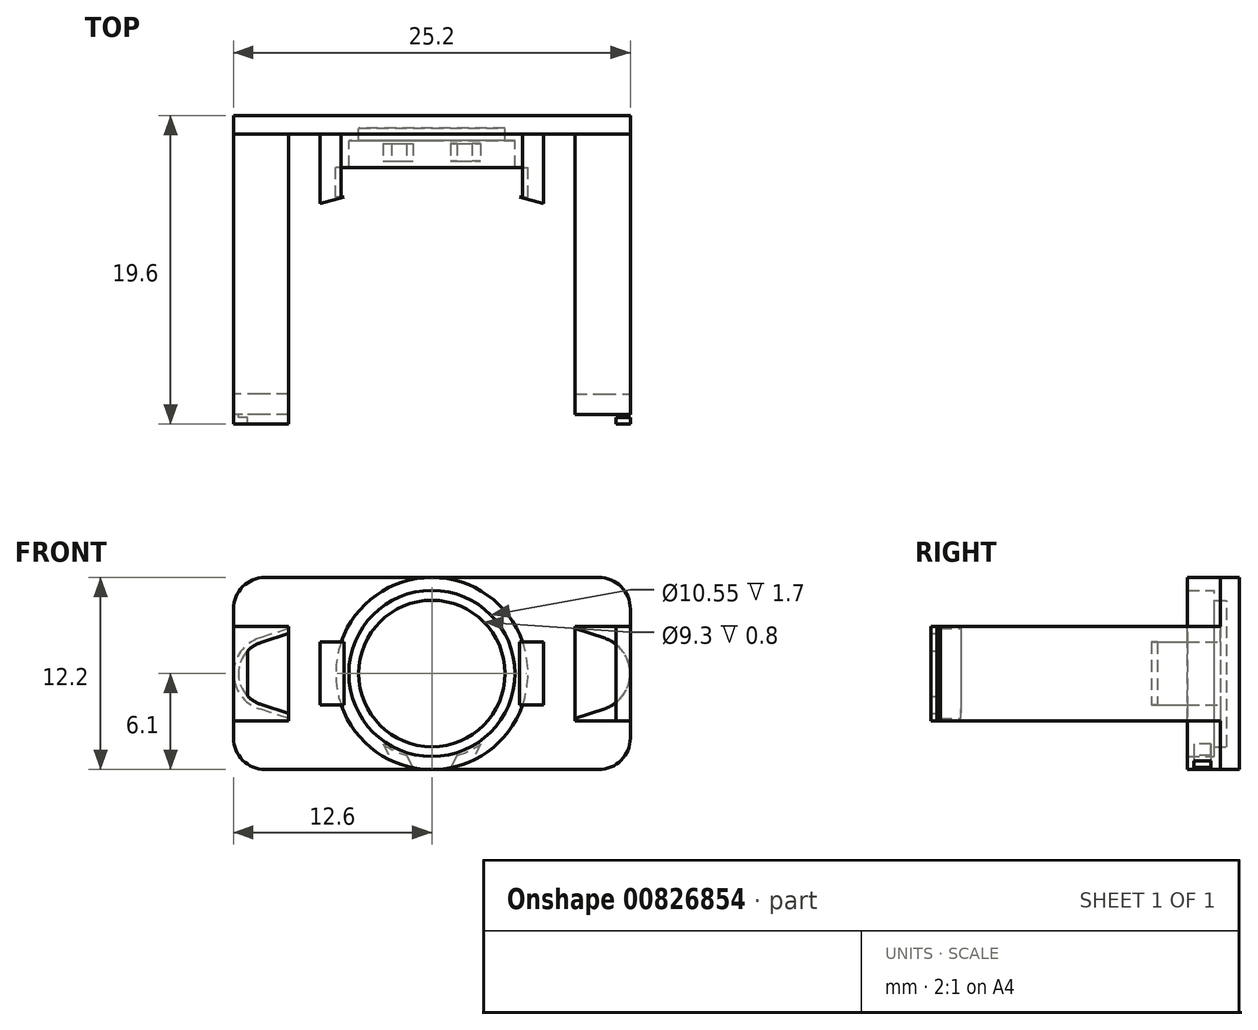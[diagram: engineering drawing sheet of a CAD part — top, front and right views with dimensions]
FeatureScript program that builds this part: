
annotation { "Feature Type Name" : "Feature", "Feature Type Description" : "" }
export const myFeature = defineFeature(function(context is Context, id is Id, definition is map)
    precondition{}
    {
        {
            var Q0;
            Q0=qCreatedBy(makeId("Front.planeOp"),FACE);
            var sketch = newSketch(context, id + "F0", { "sketchPlane" : qUnion([Q0])});
            skCircle(sketch, "E0", {"center": v(0, 0) * mm, "radius": 5 * mm});
            skCircle(sketch, "E1", {"center": v(0, 0) * mm, "radius": 6.1 * mm});
            skSolve(sketch);
        }
        {
            var Q0;
            Q0=makeQuery(id+"F0.imprint","IMPRINT",FACE,{"disambiguationData":[TD([[makeQuery(id+"F0.imprint","IMPRINT",EDGE,{"derivedFrom":sQuery(id+"F0.wireOp",EDGE,"E0")}),-1.0]])]});
            var Q1;
            Q1=makeQuery(id+"F0.imprint","IMPRINT",FACE,{"disambiguationData":[TD([[makeQuery(id+"F0.imprint","IMPRINT",EDGE,{"derivedFrom":sQuery(id+"F0.wireOp",EDGE,"E0")}),1.0]])]});
            extrude(context, id + "F1", {"entities" : qUnion([Q0, Q1]), "depth" : 0.8 * mm, "offsetDistance" : 25 * mm});
        }
        {
            var Q0;
            Q0=makeQuery(id+"F1.opExtrude","CAP_FACE",FACE,{"disambiguationData":[OSD([sQuery(id+"F0.wireOp",EDGE,"E1")])],"isStart":false});
            var sketch = newSketch(context, id + "F2", { "sketchPlane" : qUnion([Q0])});
            skCircle(sketch, "E2", {"center": v(0, 0) * mm, "radius": 5.45 * mm});
            skCircle(sketch, "E3", {"center": v(0, 0) * mm, "radius": 6.1 * mm});
            skSolve(sketch);
        }
        {
            var Q0;
            Q0=makeQuery(id+"F2.imprint","IMPRINT",FACE,{"disambiguationData":[TD([[makeQuery(id+"F2.imprint","IMPRINT",EDGE,{"derivedFrom":sQuery(id+"F2.wireOp",EDGE,"E2")}),-1.0]])]});
            extrude(context, id + "F3", {"entities" : qUnion([Q0]), "operationType" : NewBodyOperationType.ADD, "depth" : 2.5 * mm, "offsetDistance" : 25 * mm});
        }
        {
            var Q0;
            Q0=makeQuery(id+"F1.opExtrude","CAP_FACE",FACE,{"disambiguationData":[OSD([sQuery(id+"F0.wireOp",EDGE,"E1")])],"isStart":false});
            var sketch = newSketch(context, id + "F4", { "sketchPlane" : qUnion([Q0])});
            skCircle(sketch, "E4", {"center": v(0, 0) * mm, "radius": 4.65 * mm});
            skSolve(sketch);
        }
        {
            var Q0;
            Q0=makeQuery(id+"F4.imprint","IMPRINT",FACE,{"disambiguationData":[TD([[makeQuery(id+"F4.imprint","IMPRINT",EDGE,{"derivedFrom":sQuery(id+"F4.wireOp",EDGE,"E4")}),-1.0]])]});
            extrude(context, id + "F5", {"entities" : qUnion([Q0]), "operationType" : NewBodyOperationType.ADD, "depth" : 0.8 * mm, "offsetDistance" : 25 * mm});
        }
        {
            var Q0;
            Q0=makeQuery(id+"F3.opExtrude","CAP_FACE",FACE,{"disambiguationData":[OSD([sQuery(id+"F2.wireOp",EDGE,"E2"),sQuery(id+"F2.wireOp",EDGE,"E3")])],"isStart":false});
            var sketch = newSketch(context, id + "F6", { "sketchPlane" : qUnion([Q0])});
            skLineSegment(sketch, "E5", {"start": v(-1.6, -5.2) * mm, "end": v(-1.2, -5.98) * mm});
            skLineSegment(sketch, "E6", {"start": v(-3.1, -4.48) * mm, "end": v(-2.56, -5.54) * mm});
            skLineSegment(sketch, "E7.MirrorCS", {"start": v(1.6, -5.2) * mm, "end": v(1.2, -5.98) * mm});
            skLineSegment(sketch, "E8.MirrorCS", {"start": v(3.1, -4.48) * mm, "end": v(2.56, -5.54) * mm});
            skCircle(sketch, "E9.0", {"center": v(0, 0) * mm, "radius": 5.45 * mm});
            skSolve(sketch);
        }
        {
            var Q0;
            {var subQ0=sQuery(id+"F6.wireOp",EDGE,"E5");Q0=makeQuery(id+"F6.imprint","IMPRINT",FACE,{"disambiguationData":[TD([[makeQuery(id+"F6.imprint","IMPRINT",EDGE,{"derivedFrom":subQ0}),-1.0]])]});}
            var Q1;
            {var subQ0=sQuery(id+"F6.wireOp",EDGE,"E7.MirrorCS");Q1=makeQuery(id+"F6.imprint","IMPRINT",FACE,{"disambiguationData":[TD([[makeQuery(id+"F6.imprint","IMPRINT",EDGE,{"derivedFrom":subQ0}),1.0]])]});}
            extrude(context, id + "F7", {"entities" : qUnion([Q0, Q1]), "operationType" : NewBodyOperationType.REMOVE, "oppositeDirection" : true, "depth" : 1.5 * mm, "offsetDistance" : 25 * mm});
        }
        {
            var Q0;
            {var subQ0=sQuery(id+"F2.wireOp",EDGE,"E3");var subQ1=sQuery(id+"F2.wireOp",EDGE,"E2");Q0=makeQuery(id+"F7.boolean.opBoolean","SPLIT",FACE,{"disambiguationData":[TD([makeQuery(id+"F7.opExtrude","SWEPT_FACE",FACE,{"disambiguationData":[OSD([sQuery(id+"F6.wireOp",EDGE,"E6")])]})])],"derivedFrom":makeQuery(id+"F3.opExtrude","CAP_FACE",FACE,{"disambiguationData":[OSD([subQ1,subQ0])],"isStart":false})});}
            var sketch = newSketch(context, id + "F8", { "sketchPlane" : qUnion([Q0])});
            skArc(sketch, "E10", {"start": v(-2.56, -5.54) * mm, "mid": v(-1.9, -5.8) * mm, "end": v(-1.2, -5.98) * mm});
            skLineSegment(sketch, "E11", {"start": v(-3.1, -4.48) * mm, "end": v(-2.56, -5.54) * mm});
            skLineSegment(sketch, "E12", {"start": v(-1.6, -5.2) * mm, "end": v(-1.2, -5.98) * mm});
            skLineSegment(sketch, "E13.MirrorCS", {"start": v(3.1, -4.48) * mm, "end": v(2.56, -5.54) * mm});
            skArc(sketch, "E14.MirrorCS", {"start": v(2.56, -5.54) * mm, "mid": v(1.9, -5.8) * mm, "end": v(1.2, -5.98) * mm});
            skLineSegment(sketch, "E15.MirrorCS", {"start": v(1.6, -5.2) * mm, "end": v(1.2, -5.98) * mm});
            skPoint(sketch, "E16.MirrorCS.end.orphan", {"position": v(1.6, -5.2) * mm});
            skPoint(sketch, "E16.MirrorCS.start.orphan", {"position": v(3.1, -4.48) * mm});
            skPoint(sketch, "E17.MirrorCS.end.orphan", {"position": v(-3.1, -4.48) * mm});
            skPoint(sketch, "E17.MirrorCS.start.orphan", {"position": v(-1.6, -5.2) * mm});
            skSolve(sketch);
        }
        {
            var Q0;
            {var subQ0=sQuery(id+"F6.wireOp",EDGE,"E5");Q0=makeQuery(id+"F6.imprint","IMPRINT",FACE,{"disambiguationData":[TD([[makeQuery(id+"F6.imprint","IMPRINT",EDGE,{"derivedFrom":subQ0}),-1.0]])]});}
            var Q1;
            {var subQ0=sQuery(id+"F6.wireOp",EDGE,"E7.MirrorCS");Q1=makeQuery(id+"F6.imprint","IMPRINT",FACE,{"disambiguationData":[TD([[makeQuery(id+"F6.imprint","IMPRINT",EDGE,{"derivedFrom":subQ0}),1.0]])]});}
            extrude(context, id + "F9", {"entities" : qUnion([Q0, Q1]), "operationType" : NewBodyOperationType.ADD, "oppositeDirection" : true, "depth" : 0.4 * mm, "offsetDistance" : 25 * mm});
        }
        {
            var Q0;
            Q0=makeQuery(id+"F1.opExtrude","CAP_FACE",FACE,{"disambiguationData":[OSD([sQuery(id+"F0.wireOp",EDGE,"E1")])],"isStart":true});
            var sketch = newSketch(context, id + "F10", { "sketchPlane" : qUnion([Q0])});
            skLineSegment(sketch, "E18.bottom", {"start": v(-12.6, -6.1) * mm, "end": v(12.6, -6.1) * mm});
            skLineSegment(sketch, "E18.top", {"start": v(-12.6, 6.1) * mm, "end": v(12.6, 6.1) * mm});
            skLineSegment(sketch, "E18.left", {"start": v(-12.6, -6.1) * mm, "end": v(-12.6, 6.1) * mm});
            skLineSegment(sketch, "E18.right", {"start": v(12.6, -6.1) * mm, "end": v(12.6, 6.1) * mm});
            skPoint(sketch, "E18.middle", {"position": v(0, 0) * mm});
            skSolve(sketch);
        }
        {
            var Q0;
            {var subQ0=sQuery(id+"F10.wireOp",EDGE,"E18.right");Q0=makeQuery(id+"F10.imprint","IMPRINT",FACE,{"disambiguationData":[TD([[makeQuery(id+"F10.imprint","IMPRINT",EDGE,{"derivedFrom":subQ0}),1.0]])]});}
            var Q1;
            {var subQ0=sQuery(id+"F10.wireOp",EDGE,"E18.left");Q1=makeQuery(id+"F10.imprint","IMPRINT",FACE,{"disambiguationData":[TD([[makeQuery(id+"F10.imprint","IMPRINT",EDGE,{"derivedFrom":subQ0}),-1.0]])]});}
            extrude(context, id + "F11", {"entities" : qUnion([Q0, Q1]), "operationType" : NewBodyOperationType.ADD, "oppositeDirection" : true, "depth" : 1.2 * mm, "offsetDistance" : 25 * mm});
        }
        {
            var Q0;
            Q0=makeQuery(id+"F11.opExtrude","SWEPT_EDGE",EDGE,{"disambiguationData":[OSD([sQuery(id+"F10.wireOp",EDGE,"E18.bottom"),sQuery(id+"F10.wireOp",EDGE,"E18.right")])]});
            var Q1;
            Q1=makeQuery(id+"F11.opExtrude","SWEPT_EDGE",EDGE,{"disambiguationData":[OSD([sQuery(id+"F10.wireOp",EDGE,"E18.bottom"),sQuery(id+"F10.wireOp",EDGE,"E18.left")])]});
            var Q2;
            Q2=makeQuery(id+"F11.opExtrude","SWEPT_EDGE",EDGE,{"disambiguationData":[OSD([sQuery(id+"F10.wireOp",EDGE,"E18.top"),sQuery(id+"F10.wireOp",EDGE,"E18.left")])]});
            var Q3;
            Q3=makeQuery(id+"F11.opExtrude","SWEPT_EDGE",EDGE,{"disambiguationData":[OSD([sQuery(id+"F10.wireOp",EDGE,"E18.top"),sQuery(id+"F10.wireOp",EDGE,"E18.right")])]});
            fillet(context, id + "F12", {"entities" : qUnion([Q0, Q1, Q2, Q3]), "radius" : 2 * mm, "tangentPropagation" : true, "allowEdgeOverflow" : false});
        }
        {
            var Q0;
            Q0=makeQuery(id+"F11.opExtrude","CAP_FACE",FACE,{"disambiguationData":[OSD([sQuery(id+"F0.wireOp",EDGE,"E1"),sQuery(id+"F10.wireOp",EDGE,"E18.bottom"),sQuery(id+"F10.wireOp",EDGE,"E18.top"),sQuery(id+"F10.wireOp",EDGE,"E18.right")])],"isStart":false});
            var sketch = newSketch(context, id + "F13", { "sketchPlane" : qUnion([Q0])});
            skLineSegment(sketch, "E19", {"start": v(-12.6, 3) * mm, "end": v(-9.1, 3) * mm});
            skLineSegment(sketch, "E20", {"start": v(-9.1, 3) * mm, "end": v(-9.1, -3) * mm});
            skLineSegment(sketch, "E21", {"start": v(-9.1, -3) * mm, "end": v(-12.6, -3) * mm});
            skLineSegment(sketch, "E22", {"start": v(-7.1, 2) * mm, "end": v(-7.1, -2) * mm});
            skLineSegment(sketch, "E23", {"start": v(-7.1, -2) * mm, "end": v(-5.76, -2) * mm});
            skLineSegment(sketch, "E24", {"start": v(-7.1, 2) * mm, "end": v(-5.76, 2) * mm});
            skSolve(sketch);
        }
        {
            var Q0;
            {var subQ0=sQuery(id+"F13.wireOp",EDGE,"E19");Q0=makeQuery(id+"F13.imprint","IMPRINT",FACE,{"disambiguationData":[TD([[makeQuery(id+"F13.imprint","IMPRINT",EDGE,{"derivedFrom":subQ0}),-1.0]])]});}
            extrude(context, id + "F14", {"entities" : qUnion([Q0]), "operationType" : NewBodyOperationType.ADD, "depth" : 16.5 * mm, "offsetDistance" : 25 * mm});
        }
        {
            var Q0;
            Q0=makeQuery(id+"F11.opExtrude","CAP_FACE",FACE,{"disambiguationData":[OSD([sQuery(id+"F0.wireOp",EDGE,"E1"),sQuery(id+"F10.wireOp",EDGE,"E18.bottom"),sQuery(id+"F10.wireOp",EDGE,"E18.top"),sQuery(id+"F10.wireOp",EDGE,"E18.left")])],"isStart":false});
            var sketch = newSketch(context, id + "F15", { "sketchPlane" : qUnion([Q0])});
            skLineSegment(sketch, "E25", {"start": v(12.6, 3) * mm, "end": v(9.1, 3) * mm});
            skLineSegment(sketch, "E26", {"start": v(9.1, 3) * mm, "end": v(9.1, -3) * mm});
            skLineSegment(sketch, "E27", {"start": v(9.1, -3) * mm, "end": v(12.6, -3) * mm});
            skLineSegment(sketch, "E28", {"start": v(7.1, 2) * mm, "end": v(7.1, -2) * mm});
            skLineSegment(sketch, "E29", {"start": v(7.1, -2) * mm, "end": v(5.76, -2) * mm});
            skLineSegment(sketch, "E30", {"start": v(7.1, 2) * mm, "end": v(5.76, 2) * mm});
            skSolve(sketch);
        }
        {
            var Q0;
            {var subQ0=sQuery(id+"F15.wireOp",EDGE,"E25");Q0=makeQuery(id+"F15.imprint","IMPRINT",FACE,{"disambiguationData":[TD([[makeQuery(id+"F15.imprint","IMPRINT",EDGE,{"derivedFrom":subQ0}),1.0]])]});}
            extrude(context, id + "F16", {"entities" : qUnion([Q0]), "operationType" : NewBodyOperationType.ADD, "depth" : 16.5 * mm, "offsetDistance" : 25 * mm});
        }
        {
            var Q0;
            Q0=makeQuery(id+"F15.imprint","IMPRINT",FACE,{"disambiguationData":[TD([[makeQuery(id+"F15.imprint","IMPRINT",EDGE,{"derivedFrom":sQuery(id+"F15.wireOp",EDGE,"E28")}),-1.0]])]});
            var Q1;
            Q1=makeQuery(id+"F13.imprint","IMPRINT",FACE,{"disambiguationData":[TD([[makeQuery(id+"F13.imprint","IMPRINT",EDGE,{"derivedFrom":sQuery(id+"F13.wireOp",EDGE,"E22")}),1.0]])]});
            extrude(context, id + "F17", {"entities" : qUnion([Q0, Q1]), "operationType" : NewBodyOperationType.ADD, "depth" : 4 * mm, "offsetDistance" : 25 * mm});
        }
        {
            var Q0;
            Q0=makeQuery(id+"F17.opExtrude","SWEPT_FACE",FACE,{"disambiguationData":[OSD([sQuery(id+"F13.wireOp",EDGE,"E23")])]});
            var sketch = newSketch(context, id + "F18", { "sketchPlane" : qUnion([Q0])});
            skLineSegment(sketch, "E31", {"start": v(-7.1, 5.2) * mm, "end": v(-7.1, 5.6) * mm});
            skLineSegment(sketch, "E32", {"start": v(-5.76, 5.2) * mm, "end": v(-5.66, 5.2) * mm});
            skLineSegment(sketch, "E33", {"start": v(-5.66, 5.2) * mm, "end": v(-7.1, 5.6) * mm});
            skSolve(sketch);
        }
        {
            var Q0;
            Q0=makeQuery(id+"F18.imprint","IMPRINT",FACE,{"disambiguationData":[TD([[makeQuery(id+"F18.imprint","IMPRINT",EDGE,{"derivedFrom":sQuery(id+"F18.wireOp",EDGE,"E31")}),-1.0]])]});
            extrude(context, id + "F19", {"entities" : qUnion([Q0]), "operationType" : NewBodyOperationType.ADD, "oppositeDirection" : true, "depth" : 4 * mm, "offsetDistance" : 25 * mm});
        }
        {
            var Q0;
            Q0=makeQuery(id+"F17.opExtrude","SWEPT_FACE",FACE,{"disambiguationData":[OSD([sQuery(id+"F15.wireOp",EDGE,"E29")])]});
            var sketch = newSketch(context, id + "F20", { "sketchPlane" : qUnion([Q0])});
            skLineSegment(sketch, "E34", {"start": v(7.1, 5.2) * mm, "end": v(7.1, 5.6) * mm});
            skLineSegment(sketch, "E35", {"start": v(5.76, 5.2) * mm, "end": v(5.66, 5.2) * mm});
            skLineSegment(sketch, "E36", {"start": v(5.66, 5.2) * mm, "end": v(7.1, 5.6) * mm});
            skSolve(sketch);
        }
        {
            var Q0;
            Q0=makeQuery(id+"F20.imprint","IMPRINT",FACE,{"disambiguationData":[TD([[makeQuery(id+"F20.imprint","IMPRINT",EDGE,{"derivedFrom":sQuery(id+"F20.wireOp",EDGE,"E34")}),1.0]])]});
            extrude(context, id + "F21", {"entities" : qUnion([Q0]), "operationType" : NewBodyOperationType.ADD, "oppositeDirection" : true, "depth" : 4 * mm, "offsetDistance" : 25 * mm});
        }
        {
            var Q0;
            {var subQ0=sQuery(id+"F13.wireOp",EDGE,"E23");Q0=makeQuery(id+"F19.boolean.opBoolean","MERGE",FACE,{"derivedFrom":[makeQuery(id+"F17.opExtrude","SWEPT_FACE",FACE,{"disambiguationData":[OSD([subQ0])]}),makeQuery(id+"F19.opExtrude","CAP_FACE",FACE,{"disambiguationData":[OSD([subQ0,sQuery(id+"F18.wireOp",EDGE,"E31"),sQuery(id+"F18.wireOp",EDGE,"scbSYdZa-IKE8-HjIA-PmpS-5iz6sRiiHXsu")])],"isStart":true})]});}
            var sketch = newSketch(context, id + "F22", { "sketchPlane" : qUnion([Q0])});
            skLineSegment(sketch, "E37", {"start": v(-5.76, 5.2) * mm, "end": v(-5.56, 5.2) * mm});
            skLineSegment(sketch, "E38", {"start": v(-5.56, 5.2) * mm, "end": v(-7.1, 5.6) * mm});
            skSolve(sketch);
        }
        {
            var Q0;
            Q0=makeQuery(id+"F22.imprint","IMPRINT",FACE,{"disambiguationData":[TD([[makeQuery(id+"F22.imprint","IMPRINT",EDGE,{"derivedFrom":sQuery(id+"F22.wireOp",EDGE,"E37")}),1.0]])]});
            extrude(context, id + "F23", {"entities" : qUnion([Q0]), "operationType" : NewBodyOperationType.ADD, "oppositeDirection" : true, "depth" : 4 * mm, "offsetDistance" : 25 * mm});
        }
        {
            var Q0;
            {var subQ0=sQuery(id+"F15.wireOp",EDGE,"E29");Q0=makeQuery(id+"F21.boolean.opBoolean","MERGE",FACE,{"derivedFrom":[makeQuery(id+"F17.opExtrude","SWEPT_FACE",FACE,{"disambiguationData":[OSD([subQ0])]}),makeQuery(id+"F21.opExtrude","CAP_FACE",FACE,{"disambiguationData":[OSD([subQ0,sQuery(id+"F20.wireOp",EDGE,"E34"),sQuery(id+"F20.wireOp",EDGE,"OUZQXp2e-nWsZ-sgYy-KXVV-Yu3MqT17kAb9")])],"isStart":true})]});}
            var sketch = newSketch(context, id + "F24", { "sketchPlane" : qUnion([Q0])});
            skLineSegment(sketch, "E39", {"start": v(5.76, 5.2) * mm, "end": v(5.56, 5.2) * mm});
            skLineSegment(sketch, "E40", {"start": v(5.56, 5.2) * mm, "end": v(7.1, 5.6) * mm});
            skSolve(sketch);
        }
        {
            var Q0;
            Q0=makeQuery(id+"F24.imprint","IMPRINT",FACE,{"disambiguationData":[TD([[makeQuery(id+"F24.imprint","IMPRINT",EDGE,{"derivedFrom":sQuery(id+"F24.wireOp",EDGE,"E39")}),-1.0]])]});
            extrude(context, id + "F25", {"entities" : qUnion([Q0]), "operationType" : NewBodyOperationType.ADD, "oppositeDirection" : true, "depth" : 4 * mm, "offsetDistance" : 25 * mm});
        }
        {
            var Q0;
            Q0=makeQuery(id+"F16.opExtrude","CAP_FACE",FACE,{"disambiguationData":[OSD([sQuery(id+"F10.wireOp",EDGE,"E18.left"),sQuery(id+"F15.wireOp",EDGE,"E25"),sQuery(id+"F15.wireOp",EDGE,"E26"),sQuery(id+"F15.wireOp",EDGE,"E27")])],"isStart":false});
            var sketch = newSketch(context, id + "F26", { "sketchPlane" : qUnion([Q0])});
            skLineSegment(sketch, "E41", {"start": v(9.1, 2.85) * mm, "end": v(10.95, 2.25) * mm});
            skArc(sketch, "E42", {"start": v(10.95, -2.25) * mm, "mid": v(12.59, 0) * mm, "end": v(10.95, 2.25) * mm});
            skLineSegment(sketch, "E43.MirrorCS", {"start": v(9.1, -2.85) * mm, "end": v(10.95, -2.25) * mm});
            skSolve(sketch);
        }
        {
            var Q0;
            {var subQ2=sQuery(id+"F26.wireOp",EDGE,"E41");Q0=makeQuery(id+"F26.imprint","IMPRINT",FACE,{"disambiguationData":[TD([[makeQuery(id+"F26.imprint","IMPRINT",EDGE,{"derivedFrom":subQ2}),1.0]])]});}
            extrude(context, id + "F27", {"entities" : qUnion([Q0]), "operationType" : NewBodyOperationType.ADD, "depth" : 1.3 * mm, "offsetDistance" : 25 * mm});
        }
        {
            var Q0;
            Q0=makeQuery(id+"F14.opExtrude","CAP_FACE",FACE,{"disambiguationData":[OSD([sQuery(id+"F10.wireOp",EDGE,"E18.right"),sQuery(id+"F13.wireOp",EDGE,"E19"),sQuery(id+"F13.wireOp",EDGE,"E20"),sQuery(id+"F13.wireOp",EDGE,"E21")])],"isStart":false});
            var sketch = newSketch(context, id + "F28", { "sketchPlane" : qUnion([Q0])});
            skLineSegment(sketch, "E44", {"start": v(-9.1, 2.85) * mm, "end": v(-10.95, 2.25) * mm});
            skLineSegment(sketch, "E45.MirrorCS", {"start": v(-9.1, -2.85) * mm, "end": v(-10.95, -2.25) * mm});
            skArc(sketch, "E46", {"start": v(-10.95, 2.25) * mm, "mid": v(-12.59, 0) * mm, "end": v(-10.95, -2.25) * mm});
            skSolve(sketch);
        }
        {
            var Q0;
            {var subQ2=sQuery(id+"F28.wireOp",EDGE,"E44");Q0=makeQuery(id+"F28.imprint","IMPRINT",FACE,{"disambiguationData":[TD([[makeQuery(id+"F28.imprint","IMPRINT",EDGE,{"derivedFrom":subQ2}),-1.0]])]});}
            extrude(context, id + "F29", {"entities" : qUnion([Q0]), "operationType" : NewBodyOperationType.ADD, "depth" : 1.3 * mm, "offsetDistance" : 25 * mm});
        }
        {
            var Q0;
            Q0=makeQuery(id+"F5.opExtrude","CAP_FACE",FACE,{"disambiguationData":[OSD([sQuery(id+"F2.wireOp",EDGE,"E2"),sQuery(id+"F4.wireOp",EDGE,"E4")])],"isStart":false});
            var sketch = newSketch(context, id + "F30", { "sketchPlane" : qUnion([Q0])});
            skCircle(sketch, "E47", {"center": v(0, 0) * mm, "radius": 5.28 * mm});
            skSolve(sketch);
        }
        {
            var Q0;
            Q0=makeQuery(id+"F30.imprint","IMPRINT",FACE,{"disambiguationData":[TD([[makeQuery(id+"F30.imprint","IMPRINT",EDGE,{"derivedFrom":sQuery(id+"F30.wireOp",EDGE,"E47")}),-1.0]])]});
            extrude(context, id + "F31", {"entities" : qUnion([Q0]), "operationType" : NewBodyOperationType.ADD, "depth" : 1.7 * mm, "offsetDistance" : 25 * mm});
        }
        {
            var Q0;
            Q0=makeQuery(id+"F29.opExtrude","CAP_FACE",FACE,{"disambiguationData":[OSD([sQuery(id+"F10.wireOp",EDGE,"E18.right"),sQuery(id+"F13.wireOp",EDGE,"E19"),sQuery(id+"F13.wireOp",EDGE,"E20"),sQuery(id+"F13.wireOp",EDGE,"E21"),sQuery(id+"F28.wireOp",EDGE,"E44"),sQuery(id+"F28.wireOp",EDGE,"E45.MirrorCS"),sQuery(id+"F28.wireOp",EDGE,"E46")])],"isStart":false});
            var sketch = newSketch(context, id + "F32", { "sketchPlane" : qUnion([Q0])});
            skLineSegment(sketch, "E48", {"start": v(-12.6, 3) * mm, "end": v(-12.6, -3) * mm});
            skLineSegment(sketch, "E49", {"start": v(-12.6, -3) * mm, "end": v(-9.1, -3) * mm});
            skLineSegment(sketch, "E50.0", {"start": v(-9.1, -2.53) * mm, "end": v(-10.86, -1.96) * mm});
            skArc(sketch, "E50.1", {"start": v(-10.86, 1.96) * mm, "mid": v(-12.3, 0) * mm, "end": v(-10.86, -1.96) * mm});
            skLineSegment(sketch, "E50.2", {"start": v(-9.1, 2.53) * mm, "end": v(-10.86, 1.96) * mm});
            skArc(sketch, "E51.MirrorCS", {"start": v(10.86, 1.96) * mm, "mid": v(12.3, 0) * mm, "end": v(10.86, -1.96) * mm});
            skLineSegment(sketch, "E52.MirrorCS", {"start": v(9.1, 2.53) * mm, "end": v(10.86, 1.96) * mm});
            skLineSegment(sketch, "E53.MirrorCS", {"start": v(9.1, -2.53) * mm, "end": v(10.86, -1.96) * mm});
            skLineSegment(sketch, "E54.MirrorCS", {"start": v(12.6, -3) * mm, "end": v(9.1, -3) * mm});
            skLineSegment(sketch, "E55.MirrorCS", {"start": v(12.6, 3) * mm, "end": v(12.6, -3) * mm});
            skLineSegment(sketch, "E56", {"start": v(-12.6, 3) * mm, "end": v(-9.1, 3) * mm});
            skLineSegment(sketch, "E57.MirrorCS", {"start": v(12.6, 3) * mm, "end": v(9.1, 3) * mm});
            skLineSegment(sketch, "E58", {"start": v(-9.1, 2.53) * mm, "end": v(-9.1, 3) * mm});
            skLineSegment(sketch, "E59", {"start": v(-9.1, -2.53) * mm, "end": v(-9.1, -3) * mm});
            skLineSegment(sketch, "E60.MirrorCS", {"start": v(9.1, -2.53) * mm, "end": v(9.1, -3) * mm});
            skLineSegment(sketch, "E61.MirrorCS", {"start": v(9.1, 2.53) * mm, "end": v(9.1, 3) * mm});
            skSolve(sketch);
        }
        {
            var Q0;
            {var subQ3=sQuery(id+"F32.wireOp",EDGE,"E50.0");Q0=makeQuery(id+"F32.imprint","IMPRINT",FACE,{"disambiguationData":[TD([[makeQuery(id+"F32.imprint","IMPRINT",EDGE,{"derivedFrom":subQ3}),1.0]])]});}
            var Q1;
            Q1=makeQuery(id+"F32.imprint","IMPRINT",FACE,{"disambiguationData":[TD([[makeQuery(id+"F32.imprint","IMPRINT",EDGE,{"derivedFrom":sQuery(id+"F32.wireOp",EDGE,"E48")}),-1.0]])]});
            var Q2;
            Q2=makeQuery(id+"F32.imprint","IMPRINT",FACE,{"disambiguationData":[TD([[makeQuery(id+"F32.imprint","IMPRINT",EDGE,{"derivedFrom":sQuery(id+"F32.wireOp",EDGE,"E51.MirrorCS")}),1.0]])]});
            extrude(context, id + "F33", {"entities" : qUnion([Q0, Q1, Q2]), "operationType" : NewBodyOperationType.ADD, "depth" : 0.2 * mm, "offsetDistance" : 25 * mm});
        }
        {
            var Q0;
            Q0=makeQuery(id+"F33.opExtrude","CAP_FACE",FACE,{"disambiguationData":[OSD([sQuery(id+"F32.wireOp",EDGE,"E48"),sQuery(id+"F32.wireOp",EDGE,"E49"),sQuery(id+"F32.wireOp",EDGE,"E50.0"),sQuery(id+"F32.wireOp",EDGE,"E50.1"),sQuery(id+"F32.wireOp",EDGE,"E50.2"),sQuery(id+"F32.wireOp",EDGE,"E56"),sQuery(id+"F32.wireOp",EDGE,"E58"),sQuery(id+"F32.wireOp",EDGE,"E59")])],"isStart":false});
            var sketch = newSketch(context, id + "F34", { "sketchPlane" : qUnion([Q0])});
            skLineSegment(sketch, "E62.bottom", {"start": v(-12.6, 3) * mm, "end": v(-11.7, 3) * mm});
            skLineSegment(sketch, "E62.top", {"start": v(-12.6, -3) * mm, "end": v(-11.7, -3) * mm});
            skLineSegment(sketch, "E62.left", {"start": v(-12.6, 3) * mm, "end": v(-12.6, -3) * mm});
            skLineSegment(sketch, "E62.right", {"start": v(-11.7, 3) * mm, "end": v(-11.7, -3) * mm});
            skLineSegment(sketch, "E63.MirrorCS", {"start": v(11.7, 3) * mm, "end": v(11.7, -3) * mm});
            skLineSegment(sketch, "E64.MirrorCS", {"start": v(12.6, 3) * mm, "end": v(12.6, -3) * mm});
            skLineSegment(sketch, "E65.MirrorCS", {"start": v(12.6, 3) * mm, "end": v(11.7, 3) * mm});
            skLineSegment(sketch, "E66.MirrorCS", {"start": v(12.6, -3) * mm, "end": v(11.7, -3) * mm});
            skSolve(sketch);
        }
        {
            var Q0;
            {var subQ1=sQuery(id+"F34.wireOp",EDGE,"E62.bottom");Q0=makeQuery(id+"F34.imprint","IMPRINT",FACE,{"disambiguationData":[TD([[makeQuery(id+"F34.imprint","IMPRINT",EDGE,{"derivedFrom":subQ1}),-1.0]])]});}
            var Q1;
            {var subQ0=sQuery(id+"F34.wireOp",EDGE,"E62.right");var subQ1=makeQuery(id+"F33.opExtrude","CAP_EDGE",EDGE,{"disambiguationData":[OSD([sQuery(id+"F32.wireOp",EDGE,"E50.1")])],"isStart":false});var subQ2=makeQuery(id+"F34.imprint","INTERSECT",VERTEX,{"disambiguationData":[OD(0.0)],"derivedFrom":[subQ1,subQ0]});Q1=makeQuery(id+"F34.imprint","IMPRINT",FACE,{"disambiguationData":[TD([[makeQuery(id+"F34.imprint","IMPRINT",EDGE,{"disambiguationData":[TD([[subQ2,-1.0]])],"derivedFrom":subQ0}),-1.0]])]});}
            var Q2;
            Q2=makeQuery(id+"F34.imprint","IMPRINT",FACE,{"disambiguationData":[TD([[makeQuery(id+"F34.imprint","IMPRINT",EDGE,{"derivedFrom":sQuery(id+"F34.wireOp",EDGE,"E63.MirrorCS")}),1.0]])]});
            var Q3;
            {var subQ6=makeQuery(id+"F33.opExtrude","CAP_EDGE",EDGE,{"disambiguationData":[OSD([sQuery(id+"F32.wireOp",EDGE,"E50.2")])],"isStart":false});Q3=makeQuery(id+"F34.imprint","IMPRINT",FACE,{"disambiguationData":[TD([[makeQuery(id+"F34.imprint","IMPRINT",EDGE,{"derivedFrom":subQ6}),-1.0]])]});}
            var Q4;
            {var subQ0=makeQuery(id+"F33.opExtrude","CAP_EDGE",EDGE,{"disambiguationData":[OSD([sQuery(id+"F32.wireOp",EDGE,"E50.0")])],"isStart":false});Q4=makeQuery(id+"F34.imprint","IMPRINT",FACE,{"disambiguationData":[TD([[makeQuery(id+"F34.imprint","IMPRINT",EDGE,{"derivedFrom":subQ0}),1.0]])]});}
            var Q5;
            Q5=makeQuery(id+"F33.opExtrude","CAP_FACE",FACE,{"disambiguationData":[OSD([sQuery(id+"F32.wireOp",EDGE,"E51.MirrorCS"),sQuery(id+"F32.wireOp",EDGE,"E52.MirrorCS"),sQuery(id+"F32.wireOp",EDGE,"E53.MirrorCS"),sQuery(id+"F32.wireOp",EDGE,"E54.MirrorCS"),sQuery(id+"F32.wireOp",EDGE,"E55.MirrorCS"),sQuery(id+"F32.wireOp",EDGE,"E57.MirrorCS"),sQuery(id+"F32.wireOp",EDGE,"E60.MirrorCS"),sQuery(id+"F32.wireOp",EDGE,"E61.MirrorCS")])],"isStart":false});
            extrude(context, id + "F35", {"entities" : qUnion([Q0, Q1, Q2, Q3, Q4, Q5]), "operationType" : NewBodyOperationType.ADD, "depth" : 0.4 * mm, "offsetDistance" : 25 * mm});
        }
    });
